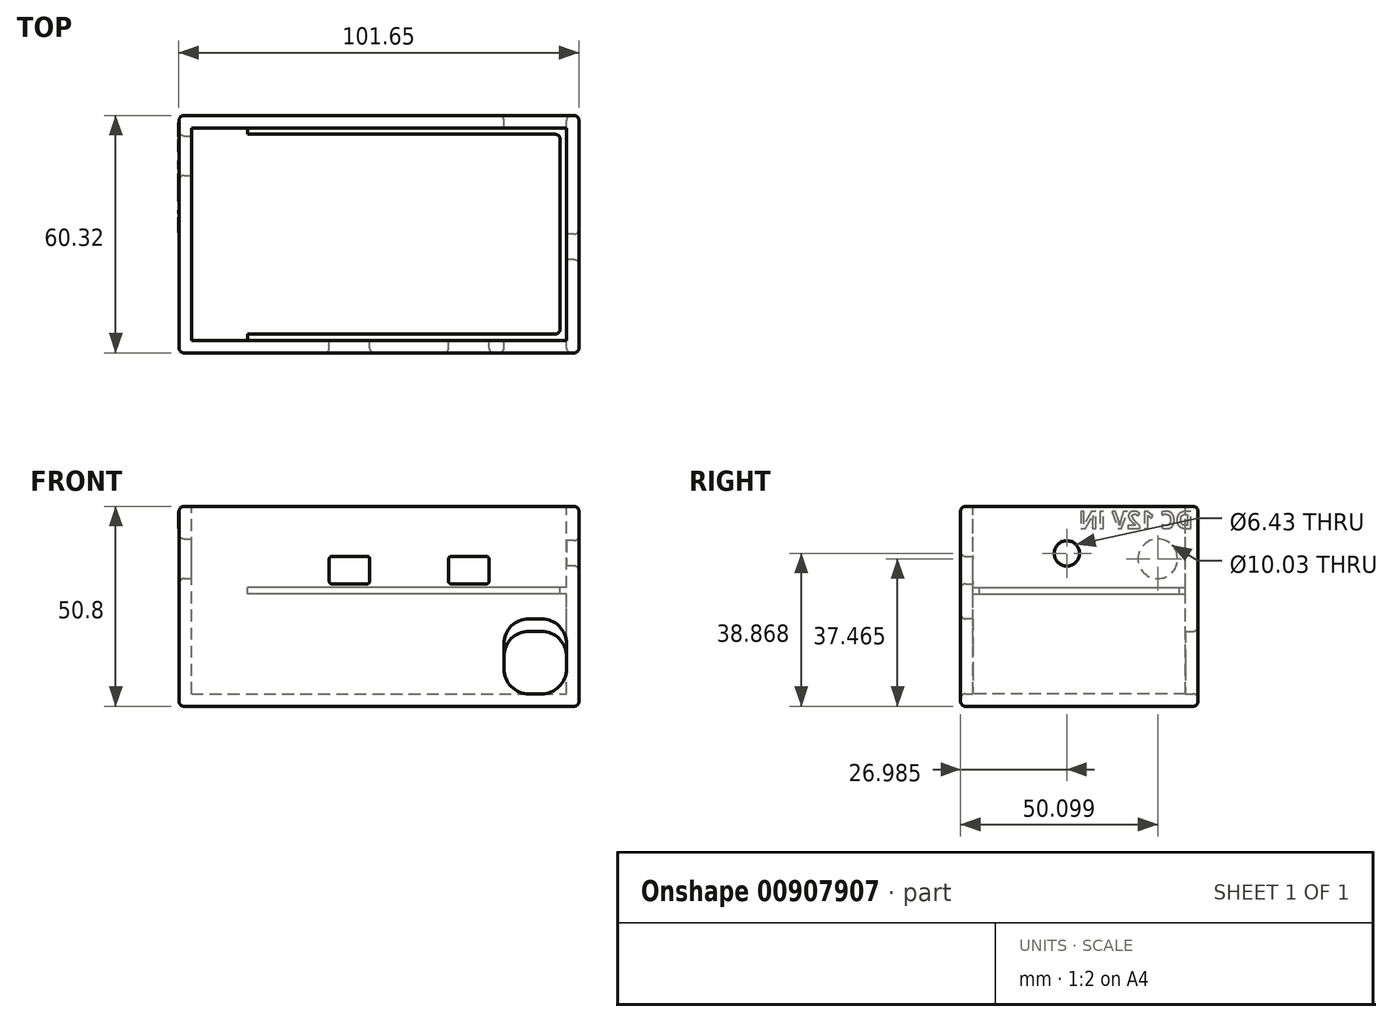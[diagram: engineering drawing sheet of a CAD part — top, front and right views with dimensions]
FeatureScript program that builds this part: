
annotation { "Feature Type Name" : "Feature", "Feature Type Description" : "" }
export const myFeature = defineFeature(function(context is Context, id is Id, definition is map)
    precondition{}
    {
        {
            var Q0;
            Q0=qCreatedBy(makeId("Top.planeOp"),FACE);
            var sketch = newSketch(context, id + "F0", { "sketchPlane" : qUnion([Q0])});
            skLineSegment(sketch, "E0.bottom", {"start": v(50.8, 30.16) * mm, "end": v(-50.8, 30.16) * mm});
            skLineSegment(sketch, "E0.top", {"start": v(50.8, -30.16) * mm, "end": v(-50.8, -30.16) * mm});
            skLineSegment(sketch, "E0.left", {"start": v(50.8, 30.16) * mm, "end": v(50.8, -30.16) * mm});
            skLineSegment(sketch, "E0.right", {"start": v(-50.8, 30.16) * mm, "end": v(-50.8, -30.16) * mm});
            skPoint(sketch, "E0.middle", {"position": v(0, 0) * mm});
            skSolve(sketch);
        }
        {
            var Q0;
            Q0 = qSketchRegion(id + "F0", true);
            extrude(context, id + "F1", {"entities" : qUnion([Q0]), "depth" : 50.8 * mm, "offsetDistance" : 25.4 * mm});
        }
        {
            var Q0;
            Q0=makeQuery(id+"F1.opExtrude","CAP_FACE",FACE,{"disambiguationData":[OSD([sQuery(id+"F0.wireOp",EDGE,"E0.bottom"),sQuery(id+"F0.wireOp",EDGE,"E0.top"),sQuery(id+"F0.wireOp",EDGE,"E0.left"),sQuery(id+"F0.wireOp",EDGE,"E0.right")])],"isStart":false});
            var sketch = newSketch(context, id + "F2", { "sketchPlane" : qUnion([Q0])});
            skLineSegment(sketch, "E1", {"start": v(-50.8, 30.16) * mm, "end": v(-50.8, 26.99) * mm});
            skLineSegment(sketch, "E2", {"start": v(-50.8, -30.16) * mm, "end": v(-50.8, -26.99) * mm});
            skLineSegment(sketch, "E3", {"start": v(-50.8, -30.16) * mm, "end": v(-47.63, -30.16) * mm});
            skLineSegment(sketch, "E4", {"start": v(50.8, 30.16) * mm, "end": v(47.63, 30.16) * mm});
            skLineSegment(sketch, "E5", {"start": v(-50.8, 26.99) * mm, "end": v(50.8, 26.99) * mm});
            skLineSegment(sketch, "E6", {"start": v(47.63, 30.16) * mm, "end": v(47.63, -30.16) * mm});
            skLineSegment(sketch, "E7", {"start": v(-50.8, -26.99) * mm, "end": v(50.8, -26.99) * mm});
            skLineSegment(sketch, "E8", {"start": v(-47.63, -30.16) * mm, "end": v(-47.63, 30.16) * mm});
            skSolve(sketch);
        }
        {
            var Q0;
            {var subQ0=sQuery(id+"F2.wireOp",EDGE,"E8");var subQ1=sQuery(id+"F2.wireOp",EDGE,"E5");var subQ2=makeQuery(id+"F2.imprint","INTERSECT",VERTEX,{"derivedFrom":[subQ1,subQ0]});Q0=makeQuery(id+"F2.imprint","IMPRINT",FACE,{"disambiguationData":[TD([[makeQuery(id+"F2.imprint","IMPRINT",EDGE,{"disambiguationData":[TD([[subQ2,-1.0]])],"derivedFrom":subQ1}),-1.0]])]});}
            extrude(context, id + "F3", {"entities" : qUnion([Q0]), "operationType" : NewBodyOperationType.REMOVE, "oppositeDirection" : true, "depth" : 47.62 * mm, "offsetDistance" : 25.4 * mm});
        }
        {
            var Q0;
            Q0=makeQuery(id+"F3.boolean.opBoolean","COPY",FACE,{"derivedFrom":makeQuery(id+"F3.opExtrude","SWEPT_FACE",FACE,{"disambiguationData":[OSD([sQuery(id+"F2.wireOp",EDGE,"E5")])]})});
            var sketch = newSketch(context, id + "F4", { "sketchPlane" : qUnion([Q0])});
            skLineSegment(sketch, "E9", {"start": v(41.28, 3.17) * mm, "end": v(38.1, 3.17) * mm});
            skLineSegment(sketch, "E10", {"start": v(31.75, 9.52) * mm, "end": v(31.75, 12.7) * mm});
            skLineSegment(sketch, "E11", {"start": v(38.1, 19.05) * mm, "end": v(41.28, 19.05) * mm});
            skLineSegment(sketch, "E12", {"start": v(47.63, 12.7) * mm, "end": v(47.63, 9.52) * mm});
            skPoint(sketch, "E13.visualSharp", {"position": v(31.75, 19.05) * mm});
            skArc(sketch, "E13.filletArc", {"start": v(38.1, 19.05) * mm, "mid": v(33.6, 17.2) * mm, "end": v(31.75, 12.7) * mm});
            skPoint(sketch, "E14.visualSharp", {"position": v(47.63, 19.05) * mm});
            skArc(sketch, "E14.filletArc", {"start": v(47.63, 12.7) * mm, "mid": v(45.77, 17.2) * mm, "end": v(41.28, 19.05) * mm});
            skPoint(sketch, "E15.visualSharp", {"position": v(47.63, 3.17) * mm});
            skArc(sketch, "E15.filletArc", {"start": v(41.28, 3.17) * mm, "mid": v(45.77, 5.03) * mm, "end": v(47.63, 9.52) * mm});
            skPoint(sketch, "E16.visualSharp", {"position": v(31.75, 3.17) * mm});
            skArc(sketch, "E16.filletArc", {"start": v(31.75, 9.52) * mm, "mid": v(33.6, 5.03) * mm, "end": v(38.1, 3.17) * mm});
            skSolve(sketch);
        }
        {
            var Q0;
            Q0 = qSketchRegion(id + "F4", true);
            extrude(context, id + "F5", {"entities" : qUnion([Q0]), "operationType" : NewBodyOperationType.REMOVE, "endBound" : BoundingType.SYMMETRIC, "depth" : 127 * mm, "offsetDistance" : 25.4 * mm});
        }
        {
            var Q0;
            {var subQ0=sQuery(id+"F2.wireOp",EDGE,"E8");var subQ2=sQuery(id+"F2.wireOp",EDGE,"E5");Q0=makeQuery(id+"F5.boolean.opBoolean","SPLIT",FACE,{"disambiguationData":[TD([makeQuery(id+"F3.boolean.opBoolean","COPY",FACE,{"derivedFrom":makeQuery(id+"F3.opExtrude","SWEPT_FACE",FACE,{"disambiguationData":[OSD([subQ0])]})})])],"derivedFrom":makeQuery(id+"F3.boolean.opBoolean","COPY",FACE,{"derivedFrom":makeQuery(id+"F3.opExtrude","SWEPT_FACE",FACE,{"disambiguationData":[OSD([subQ2])]})})});}
            var sketch = newSketch(context, id + "F6", { "sketchPlane" : qUnion([Q0])});
            skLineSegment(sketch, "E17", {"start": v(47.63, 12.7) * mm, "end": v(47.63, 3.17) * mm});
            skLineSegment(sketch, "E18", {"start": v(47.63, 3.17) * mm, "end": v(47.63, 28.57) * mm});
            skLineSegment(sketch, "E19", {"start": v(47.63, 28.57) * mm, "end": v(41.28, 28.57) * mm});
            skLineSegment(sketch, "E20", {"start": v(47.63, 28.57) * mm, "end": v(47.63, 30.18) * mm});
            skLineSegment(sketch, "E21", {"start": v(47.63, 30.18) * mm, "end": v(41.28, 30.18) * mm});
            skLineSegment(sketch, "E22", {"start": v(41.28, 30.18) * mm, "end": v(41.28, 28.57) * mm});
            skLineSegment(sketch, "E23", {"start": v(47.63, 28.57) * mm, "end": v(46.02, 28.57) * mm});
            skLineSegment(sketch, "E24", {"start": v(46.02, 28.57) * mm, "end": v(46.02, 3.17) * mm});
            skLineSegment(sketch, "E25", {"start": v(47.63, 30.18) * mm, "end": v(-33.32, 30.18) * mm});
            skLineSegment(sketch, "E26", {"start": v(41.28, 28.57) * mm, "end": v(-33.32, 28.57) * mm});
            skLineSegment(sketch, "E27", {"start": v(-33.32, 28.57) * mm, "end": v(-33.32, 30.18) * mm});
            skSolve(sketch);
        }
        {
            var Q0;
            Q0 = qSketchRegion(id + "F6", true);
            var Q1;
            {var subQ3=sQuery(id+"F6.wireOp",EDGE,"E23");Q1=makeQuery(id+"F6.imprint","IMPRINT",FACE,{"disambiguationData":[TD([[makeQuery(id+"F6.imprint","IMPRINT",EDGE,{"derivedFrom":subQ3}),1.0]])]});}
            extrude(context, id + "F7", {"entities" : qUnion([Q0, Q1]), "operationType" : NewBodyOperationType.ADD, "endBound" : BoundingType.UP_TO_NEXT, "depth" : 53.97 * mm, "offsetDistance" : 25.4 * mm});
        }
        {
            var Q0;
            Q0=makeQuery(id+"F7.opExtrude","SWEPT_FACE",FACE,{"disambiguationData":[OSD([sQuery(id+"F6.wireOp",EDGE,"E25")])]});
            var sketch = newSketch(context, id + "F8", { "sketchPlane" : qUnion([Q0])});
            skLineSegment(sketch, "E28", {"start": v(-33.32, 26.99) * mm, "end": v(-33.32, 25.39) * mm});
            skLineSegment(sketch, "E29", {"start": v(47.63, 25.39) * mm, "end": v(47.63, 26.99) * mm});
            skLineSegment(sketch, "E30", {"start": v(47.63, 25.39) * mm, "end": v(47.63, 20.64) * mm});
            skLineSegment(sketch, "E31", {"start": v(47.63, 26.99) * mm, "end": v(46.02, 26.99) * mm});
            skLineSegment(sketch, "E32", {"start": v(46.02, 26.99) * mm, "end": v(41.28, 26.99) * mm});
            skLineSegment(sketch, "E33", {"start": v(47.63, -26.99) * mm, "end": v(47.63, -25.39) * mm});
            skLineSegment(sketch, "E34", {"start": v(47.63, -25.39) * mm, "end": v(47.63, -20.64) * mm});
            skLineSegment(sketch, "E35", {"start": v(47.63, -26.99) * mm, "end": v(46.02, -26.99) * mm});
            skLineSegment(sketch, "E36", {"start": v(46.02, -26.99) * mm, "end": v(41.28, -26.99) * mm});
            skLineSegment(sketch, "E37", {"start": v(-33.32, -26.99) * mm, "end": v(-33.32, -25.39) * mm});
            skLineSegment(sketch, "E38", {"start": v(-33.32, -25.39) * mm, "end": v(41.27, -25.39) * mm});
            skLineSegment(sketch, "E39", {"start": v(41.27, -25.39) * mm, "end": v(44.75, -25.39) * mm});
            skLineSegment(sketch, "E40", {"start": v(46.02, -24.12) * mm, "end": v(46.02, -20.64) * mm});
            skLineSegment(sketch, "E41", {"start": v(46.02, -20.64) * mm, "end": v(46.02, 24.12) * mm});
            skLineSegment(sketch, "E42", {"start": v(44.75, 25.39) * mm, "end": v(41.28, 25.39) * mm});
            skLineSegment(sketch, "E43", {"start": v(41.28, 25.39) * mm, "end": v(-33.32, 25.39) * mm});
            skPoint(sketch, "E44.visualSharp", {"position": v(46.02, 25.39) * mm});
            skArc(sketch, "E44.filletArc", {"start": v(46.02, 24.12) * mm, "mid": v(45.65, 25.02) * mm, "end": v(44.75, 25.39) * mm});
            skPoint(sketch, "E45.visualSharp", {"position": v(46.02, -25.39) * mm});
            skArc(sketch, "E45.filletArc", {"start": v(44.75, -25.39) * mm, "mid": v(45.65, -25.02) * mm, "end": v(46.02, -24.12) * mm});
            skSolve(sketch);
        }
        {
            var Q0;
            Q0 = qSketchRegion(id + "F8", true);
            var Q1;
            {var subQ0=sQuery(id+"F8.wireOp",EDGE,"E38");Q1=makeQuery(id+"F8.imprint","IMPRINT",FACE,{"disambiguationData":[TD([[makeQuery(id+"F8.imprint","IMPRINT",EDGE,{"derivedFrom":subQ0}),1.0]])]});}
            extrude(context, id + "F9", {"entities" : qUnion([Q0, Q1]), "operationType" : NewBodyOperationType.REMOVE, "oppositeDirection" : true, "depth" : 1.6 * mm, "offsetDistance" : 25.4 * mm});
        }
        {
            var Q0;
            Q0=makeQuery(id+"F7.boolean.opBoolean","SPLIT",FACE,{"disambiguationData":[TD([makeQuery(id+"F7.opExtrude","SWEPT_FACE",FACE,{"disambiguationData":[OSD([sQuery(id+"F6.wireOp",EDGE,"E25")])]})])],"derivedFrom":makeQuery(id+"F5.boolean.opBoolean","MERGE",FACE,{"derivedFrom":[makeQuery(id+"F3.boolean.opBoolean","COPY",FACE,{"derivedFrom":makeQuery(id+"F3.opExtrude","SWEPT_FACE",FACE,{"disambiguationData":[OSD([sQuery(id+"F2.wireOp",EDGE,"E6")])]})})],"fromTools":[makeQuery(id+"F5.opExtrude","SWEPT_FACE",FACE,{"disambiguationData":[OSD([sQuery(id+"F4.wireOp",EDGE,"E12")])]})]})});
            var sketch = newSketch(context, id + "F10", { "sketchPlane" : qUnion([Q0])});
            skLineSegment(sketch, "E46", {"start": v(-26.99, 30.18) * mm, "end": v(26.99, 30.18) * mm});
            skLineSegment(sketch, "E47", {"start": v(26.99, 30.18) * mm, "end": v(7.94, 30.18) * mm});
            skLineSegment(sketch, "E48", {"start": v(7.94, 30.18) * mm, "end": v(-1.59, 30.18) * mm});
            skLineSegment(sketch, "E49", {"start": v(-1.59, 30.18) * mm, "end": v(-1.59, 42.88) * mm});
            skLineSegment(sketch, "E50", {"start": v(-1.59, 42.88) * mm, "end": v(7.94, 42.88) * mm});
            skLineSegment(sketch, "E51", {"start": v(7.94, 42.88) * mm, "end": v(7.94, 30.18) * mm});
            skLineSegment(sketch, "E52", {"start": v(3.18, 42.88) * mm, "end": v(3.18, 42.08) * mm});
            skLineSegment(sketch, "E53", {"start": v(3.18, 35.66) * mm, "end": v(3.18, 34.87) * mm});
            skCircle(sketch, "E54", {"center": v(3.18, 38.87) * mm, "radius": 3.21 * mm});
            skSolve(sketch);
        }
        {
            var Q0;
            {var subQ0=sQuery(id+"F10.wireOp",EDGE,"E54");var subQ1=makeQuery(id+"F10.imprint","IMPRINT",VERTEX,{"disambiguationData":[OD(0.0)],"derivedFrom":subQ0});Q0=makeQuery(id+"F10.imprint","IMPRINT",FACE,{"disambiguationData":[TD([[makeQuery(id+"F10.imprint","IMPRINT",EDGE,{"disambiguationData":[TD([[subQ1,-1.0]])],"derivedFrom":subQ0}),1.0]])]});}
            extrude(context, id + "F11", {"entities" : qUnion([Q0]), "operationType" : NewBodyOperationType.REMOVE, "endBound" : BoundingType.UP_TO_NEXT, "oppositeDirection" : true, "depth" : 25.4 * mm, "offsetDistance" : 25.4 * mm});
        }
        {
            var Q0;
            Q0=makeQuery(id+"F1.opExtrude","SWEPT_FACE",FACE,{"disambiguationData":[OSD([sQuery(id+"F0.wireOp",EDGE,"E0.top")])]});
            var sketch = newSketch(context, id + "F12", { "sketchPlane" : qUnion([Q0])});
            skLineSegment(sketch, "E55", {"start": v(31.75, 12.7) * mm, "end": v(31.75, 15.87) * mm});
            skLineSegment(sketch, "E56", {"start": v(47.63, 12.7) * mm, "end": v(47.63, 15.87) * mm});
            skLineSegment(sketch, "E57", {"start": v(47.63, 15.87) * mm, "end": v(47.63, 15.88) * mm});
            skLineSegment(sketch, "E58", {"start": v(41.28, 22.23) * mm, "end": v(41.28, 22.23) * mm});
            skLineSegment(sketch, "E59", {"start": v(41.28, 22.23) * mm, "end": v(38.1, 22.23) * mm});
            skLineSegment(sketch, "E60", {"start": v(38.1, 22.23) * mm, "end": v(38.1, 22.23) * mm});
            skLineSegment(sketch, "E61", {"start": v(31.75, 15.88) * mm, "end": v(31.75, 15.87) * mm});
            skPoint(sketch, "E62.visualSharp", {"position": v(31.75, 22.23) * mm});
            skArc(sketch, "E62.filletArc", {"start": v(38.1, 22.23) * mm, "mid": v(33.6, 20.37) * mm, "end": v(31.75, 15.88) * mm});
            skPoint(sketch, "E63.visualSharp", {"position": v(47.63, 22.23) * mm});
            skArc(sketch, "E63.filletArc", {"start": v(47.63, 15.88) * mm, "mid": v(45.77, 20.37) * mm, "end": v(41.28, 22.23) * mm});
            skArc(sketch, "E64", {"start": v(38.1, 19.05) * mm, "mid": v(33.6, 17.2) * mm, "end": v(31.75, 12.7) * mm});
            skArc(sketch, "E65", {"start": v(47.63, 12.7) * mm, "mid": v(45.77, 17.2) * mm, "end": v(41.28, 19.05) * mm});
            skLineSegment(sketch, "E66", {"start": v(38.1, 19.05) * mm, "end": v(41.28, 19.05) * mm});
            skSolve(sketch);
        }
        {
            var Q0;
            Q0=makeQuery(id+"F12.imprint","IMPRINT",FACE,{"disambiguationData":[TD([[makeQuery(id+"F12.imprint","IMPRINT",EDGE,{"derivedFrom":sQuery(id+"F12.wireOp",EDGE,"E55")}),-1.0]])]});
            extrude(context, id + "F13", {"entities" : qUnion([Q0]), "operationType" : NewBodyOperationType.REMOVE, "oppositeDirection" : true, "depth" : 57.15 * mm, "offsetDistance" : 25.4 * mm});
        }
        {
            var Q0;
            Q0=makeQuery(id+"F3.boolean.opBoolean","COPY",FACE,{"derivedFrom":makeQuery(id+"F3.opExtrude","SWEPT_FACE",FACE,{"disambiguationData":[OSD([sQuery(id+"F2.wireOp",EDGE,"E8")])]})});
            var sketch = newSketch(context, id + "F14", { "sketchPlane" : qUnion([Q0])});
            skLineSegment(sketch, "E67", {"start": v(26.99, 3.17) * mm, "end": v(26.99, 37.47) * mm});
            skLineSegment(sketch, "E68", {"start": v(26.99, 37.47) * mm, "end": v(24.96, 37.47) * mm});
            skLineSegment(sketch, "E69", {"start": v(24.96, 37.47) * mm, "end": v(14.92, 37.47) * mm});
            skCircle(sketch, "E70", {"center": v(19.94, 37.47) * mm, "radius": 5.02 * mm});
            skSolve(sketch);
        }
        {
            var Q0;
            {var subQ0=sQuery(id+"F14.wireOp",EDGE,"E69");Q0=makeQuery(id+"F14.imprint","IMPRINT",FACE,{"disambiguationData":[TD([[makeQuery(id+"F14.imprint","IMPRINT",EDGE,{"derivedFrom":subQ0}),-1.0]])]});}
            var Q1;
            {var subQ0=sQuery(id+"F14.wireOp",EDGE,"E69");Q1=makeQuery(id+"F14.imprint","IMPRINT",FACE,{"disambiguationData":[TD([[makeQuery(id+"F14.imprint","IMPRINT",EDGE,{"derivedFrom":subQ0}),1.0]])]});}
            extrude(context, id + "F15", {"entities" : qUnion([Q0, Q1]), "operationType" : NewBodyOperationType.REMOVE, "endBound" : BoundingType.UP_TO_NEXT, "oppositeDirection" : true, "depth" : 25.4 * mm, "offsetDistance" : 25.4 * mm});
        }
        {
            var Q0;
            Q0=makeQuery(id+"F1.opExtrude","CAP_EDGE",EDGE,{"disambiguationData":[OSD([sQuery(id+"F0.wireOp",EDGE,"E0.top")])],"isStart":false});
            var Q1;
            Q1=makeQuery(id+"F1.opExtrude","SWEPT_EDGE",EDGE,{"disambiguationData":[OSD([sQuery(id+"F0.wireOp",EDGE,"E0.top"),sQuery(id+"F0.wireOp",EDGE,"E0.right")])]});
            var Q2;
            Q2=makeQuery(id+"F1.opExtrude","CAP_EDGE",EDGE,{"disambiguationData":[OSD([sQuery(id+"F0.wireOp",EDGE,"E0.right")])],"isStart":true});
            var Q3;
            Q3=makeQuery(id+"F1.opExtrude","CAP_EDGE",EDGE,{"disambiguationData":[OSD([sQuery(id+"F0.wireOp",EDGE,"E0.top")])],"isStart":true});
            var Q4;
            Q4=makeQuery(id+"F1.opExtrude","SWEPT_EDGE",EDGE,{"disambiguationData":[OSD([sQuery(id+"F0.wireOp",EDGE,"E0.top"),sQuery(id+"F0.wireOp",EDGE,"E0.left")])]});
            var Q5;
            Q5=makeQuery(id+"F1.opExtrude","CAP_EDGE",EDGE,{"disambiguationData":[OSD([sQuery(id+"F0.wireOp",EDGE,"E0.left")])],"isStart":false});
            var Q6;
            Q6=makeQuery(id+"F1.opExtrude","CAP_EDGE",EDGE,{"disambiguationData":[OSD([sQuery(id+"F0.wireOp",EDGE,"E0.bottom")])],"isStart":false});
            var Q7;
            Q7=makeQuery(id+"F1.opExtrude","SWEPT_EDGE",EDGE,{"disambiguationData":[OSD([sQuery(id+"F0.wireOp",EDGE,"E0.bottom"),sQuery(id+"F0.wireOp",EDGE,"E0.right")])]});
            var Q8;
            Q8=makeQuery(id+"F1.opExtrude","CAP_EDGE",EDGE,{"disambiguationData":[OSD([sQuery(id+"F0.wireOp",EDGE,"E0.right")])],"isStart":false});
            var Q9;
            Q9=makeQuery(id+"F1.opExtrude","SWEPT_FACE",FACE,{"disambiguationData":[OSD([sQuery(id+"F0.wireOp",EDGE,"E0.left")])]});
            var Q10;
            Q10=makeQuery(id+"F1.opExtrude","CAP_EDGE",EDGE,{"disambiguationData":[OSD([sQuery(id+"F0.wireOp",EDGE,"E0.left")])],"isStart":true});
            var Q11;
            Q11=makeQuery(id+"F1.opExtrude","CAP_EDGE",EDGE,{"disambiguationData":[OSD([sQuery(id+"F0.wireOp",EDGE,"E0.bottom")])],"isStart":true});
            var Q12;
            Q12=makeQuery(id+"F1.opExtrude","SWEPT_FACE",FACE,{"disambiguationData":[OSD([sQuery(id+"F0.wireOp",EDGE,"E0.bottom")])]});
            var Q13;
            Q13=makeQuery(id+"F1.opExtrude","SWEPT_FACE",FACE,{"disambiguationData":[OSD([sQuery(id+"F0.wireOp",EDGE,"E0.top")])]});
            var Q14;
            Q14=makeQuery(id+"F1.opExtrude","SWEPT_FACE",FACE,{"disambiguationData":[OSD([sQuery(id+"F0.wireOp",EDGE,"E0.right")])]});
            fillet(context, id + "F16", {"entities" : qUnion([Q0, Q1, Q2, Q3, Q4, Q5, Q6, Q7, Q8, Q9, Q10, Q11, Q12, Q13, Q14]), "radius" : 1.27 * mm, "tangentPropagation" : true, "allowEdgeOverflow" : false});
        }
        {
            var Q0;
            Q0=makeQuery(id+"F1.opExtrude","SWEPT_FACE",FACE,{"disambiguationData":[OSD([sQuery(id+"F0.wireOp",EDGE,"E0.right")])]});
            var sketch = newSketch(context, id + "F17", { "sketchPlane" : qUnion([Q0])});
            skText(sketch, "E71", { "text": "DC 12V IN", "fontName": "OpenSans-Bold.ttf"});
            const initialGuessF17  = {"E71": [-0.0289, 0.0452, 1, 0, 0.00433]};
            skSetInitialGuess(sketch, initialGuessF17);
            skSolve(sketch);
        }
        {
            var Q0;
            Q0 = qSketchRegion(id + "F17", true);
            extrude(context, id + "F18", {"entities" : qUnion([Q0]), "operationType" : NewBodyOperationType.ADD, "depth" : 0.05 * mm, "offsetDistance" : 25.4 * mm});
        }
        {
            var Q0;
            {var subQ0=sQuery(id+"F2.wireOp",EDGE,"E8");var subQ1=sQuery(id+"F2.wireOp",EDGE,"E7");Q0=makeQuery(id+"F5.boolean.opBoolean","SPLIT",FACE,{"disambiguationData":[TD([makeQuery(id+"F3.boolean.opBoolean","COPY",FACE,{"derivedFrom":makeQuery(id+"F3.opExtrude","SWEPT_FACE",FACE,{"disambiguationData":[OSD([subQ0])]})})])],"derivedFrom":makeQuery(id+"F3.boolean.opBoolean","COPY",FACE,{"derivedFrom":makeQuery(id+"F3.opExtrude","SWEPT_FACE",FACE,{"disambiguationData":[OSD([subQ1])]})})});}
            var sketch = newSketch(context, id + "F19", { "sketchPlane" : qUnion([Q0])});
            skLineSegment(sketch, "E72", {"start": v(-47.63, 50.8) * mm, "end": v(-27.94, 50.8) * mm});
            skLineSegment(sketch, "E73", {"start": v(-27.94, 50.8) * mm, "end": v(-17.68, 50.8) * mm});
            skLineSegment(sketch, "E74", {"start": v(-17.68, 50.8) * mm, "end": v(2.36, 50.8) * mm});
            skLineSegment(sketch, "E75", {"start": v(2.36, 50.8) * mm, "end": v(12.62, 50.8) * mm});
            skLineSegment(sketch, "E76", {"start": v(-17.68, 50.8) * mm, "end": v(-17.68, 38.1) * mm});
            skLineSegment(sketch, "E77", {"start": v(2.36, 50.8) * mm, "end": v(2.36, 38.1) * mm});
            skLineSegment(sketch, "E78.bottom", {"start": v(-27.3, 31.12) * mm, "end": v(-18.31, 31.12) * mm});
            skLineSegment(sketch, "E78.top", {"start": v(-27.3, 38.1) * mm, "end": v(-18.31, 38.1) * mm});
            skLineSegment(sketch, "E78.left", {"start": v(-27.94, 31.75) * mm, "end": v(-27.94, 37.46) * mm});
            skLineSegment(sketch, "E78.right", {"start": v(-17.68, 31.75) * mm, "end": v(-17.68, 37.46) * mm});
            skLineSegment(sketch, "E79.bottom", {"start": v(3, 38.1) * mm, "end": v(11.99, 38.1) * mm});
            skLineSegment(sketch, "E79.top", {"start": v(3, 31.11) * mm, "end": v(11.99, 31.11) * mm});
            skLineSegment(sketch, "E79.left", {"start": v(2.36, 37.46) * mm, "end": v(2.36, 31.75) * mm});
            skLineSegment(sketch, "E79.right", {"start": v(12.62, 37.46) * mm, "end": v(12.62, 31.75) * mm});
            skLineSegment(sketch, "E80", {"start": v(-27.94, 38.1) * mm, "end": v(-27.94, 31.12) * mm});
            skLineSegment(sketch, "E81", {"start": v(-27.94, 50.8) * mm, "end": v(-27.94, 38.1) * mm});
            skPoint(sketch, "E82.visualSharp", {"position": v(-27.94, 38.1) * mm});
            skArc(sketch, "E82.filletArc", {"start": v(-27.3, 38.1) * mm, "mid": v(-27.75, 37.91) * mm, "end": v(-27.94, 37.46) * mm});
            skPoint(sketch, "E83.visualSharp", {"position": v(-17.68, 38.1) * mm});
            skArc(sketch, "E83.filletArc", {"start": v(-17.68, 37.46) * mm, "mid": v(-17.86, 37.91) * mm, "end": v(-18.31, 38.1) * mm});
            skPoint(sketch, "E84.visualSharp", {"position": v(-17.68, 31.12) * mm});
            skArc(sketch, "E84.filletArc", {"start": v(-18.31, 31.12) * mm, "mid": v(-17.86, 31.3) * mm, "end": v(-17.68, 31.75) * mm});
            skPoint(sketch, "E85.visualSharp", {"position": v(-27.94, 31.12) * mm});
            skArc(sketch, "E85.filletArc", {"start": v(-27.94, 31.75) * mm, "mid": v(-27.75, 31.3) * mm, "end": v(-27.3, 31.12) * mm});
            skLineSegment(sketch, "E86", {"start": v(12.62, 50.8) * mm, "end": v(12.62, 38.1) * mm});
            skPoint(sketch, "E87.visualSharp", {"position": v(2.36, 38.1) * mm});
            skArc(sketch, "E87.filletArc", {"start": v(3, 38.1) * mm, "mid": v(2.55, 37.91) * mm, "end": v(2.36, 37.46) * mm});
            skPoint(sketch, "E88.visualSharp", {"position": v(2.36, 31.11) * mm});
            skArc(sketch, "E88.filletArc", {"start": v(2.36, 31.75) * mm, "mid": v(2.55, 31.3) * mm, "end": v(3, 31.12) * mm});
            skPoint(sketch, "E89.visualSharp", {"position": v(12.62, 31.11) * mm});
            skArc(sketch, "E89.filletArc", {"start": v(11.99, 31.12) * mm, "mid": v(12.44, 31.3) * mm, "end": v(12.62, 31.75) * mm});
            skPoint(sketch, "E90.visualSharp", {"position": v(12.62, 38.1) * mm});
            skArc(sketch, "E90.filletArc", {"start": v(12.62, 37.46) * mm, "mid": v(12.44, 37.91) * mm, "end": v(11.99, 38.1) * mm});
            skSolve(sketch);
        }
        {
            var Q0;
            Q0 = qSketchRegion(id + "F19", true);
            extrude(context, id + "F20", {"entities" : qUnion([Q0]), "operationType" : NewBodyOperationType.REMOVE, "endBound" : BoundingType.UP_TO_NEXT, "oppositeDirection" : true, "depth" : 25.4 * mm, "offsetDistance" : 25.4 * mm});
        }
        {
            var Q0;
            Q0=makeQuery(id+"F1.opExtrude","SWEPT_FACE",FACE,{"disambiguationData":[OSD([sQuery(id+"F0.wireOp",EDGE,"E0.top")])]});
            fillet(context, id + "F21", {"entities" : qUnion([Q0]), "radius" : 1.27 * mm, "tangentPropagation" : true, "allowEdgeOverflow" : false});
        }
    });
